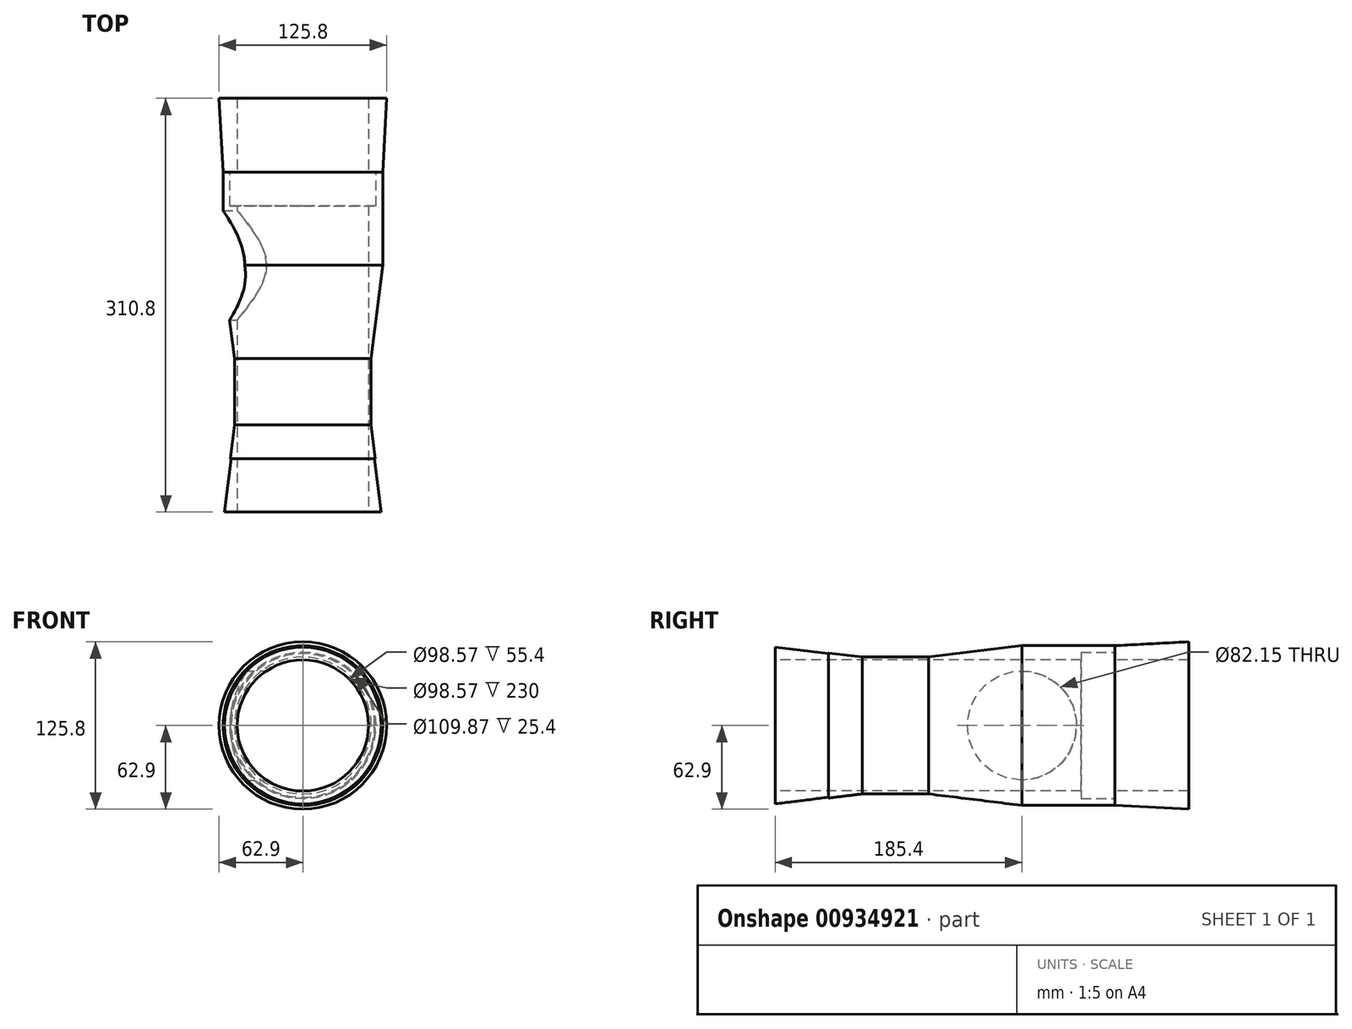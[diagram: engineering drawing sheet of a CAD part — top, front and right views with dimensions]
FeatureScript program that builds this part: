
annotation { "Feature Type Name" : "Feature", "Feature Type Description" : "" }
export const myFeature = defineFeature(function(context is Context, id is Id, definition is map)
    precondition{}
    {
        {
            var Q0;
            Q0=qCreatedBy(makeId("Front.planeOp"),FACE);
            var sketch = newSketch(context, id + "F0", { "sketchPlane" : qUnion([Q0])});
            skCircle(sketch, "E0", {"center": v(0, 0) * mm, "radius": 60 * mm});
            skSolve(sketch);
        }
        {
            var Q0;
            Q0=makeQuery(id+"F0.imprint","IMPRINT",FACE,{"disambiguationData":[TD([[makeQuery(id+"F0.imprint","IMPRINT",EDGE,{"derivedFrom":sQuery(id+"F0.wireOp",EDGE,"E0")}),1.0]])]});
            extrude(context, id + "F1", {"entities" : qUnion([Q0]), "oppositeDirection" : true, "depth" : 70 * mm, "offsetDistance" : 25.4 * mm});
        }
        {
            var Q0;
            Q0=makeQuery(id+"F1.opExtrude","CAP_FACE",FACE,{"disambiguationData":[OSD([sQuery(id+"F0.wireOp",EDGE,"E0")])],"isStart":true});
            var sketch = newSketch(context, id + "F2", { "sketchPlane" : qUnion([Q0])});
            skCircle(sketch, "E1", {"center": v(0, 0) * mm, "radius": 60 * mm});
            skSolve(sketch);
        }
        {
            var Q0;
            Q0=qSketchRegion(id+"F2",true);
            extrude(context, id + "F3", {"entities" : qUnion([Q0]), "operationType" : NewBodyOperationType.ADD, "depth" : 70 * mm, "offsetDistance" : 25.4 * mm, "hasDraft" : true, "draftAngle" : 7 * degree, "draftPullDirection" : true});
        }
        {
            var Q0;
            Q0=makeQuery(id+"F3.opExtrude","CAP_FACE",FACE,{"disambiguationData":[OSD([sQuery(id+"F2.wireOp",EDGE,"E1")])],"isStart":false});
            var sketch = newSketch(context, id + "F4", { "sketchPlane" : qUnion([Q0])});
            skCircle(sketch, "E2", {"center": v(0, 0) * mm, "radius": 53.52 * mm});
            skSolve(sketch);
        }
        {
            var Q0;
            Q0=makeQuery(id+"F1.opExtrude","CAP_FACE",FACE,{"disambiguationData":[OSD([sQuery(id+"F0.wireOp",EDGE,"E0")])],"isStart":false});
            var sketch = newSketch(context, id + "F5", { "sketchPlane" : qUnion([Q0])});
            skCircle(sketch, "E3", {"center": v(0, 0) * mm, "radius": 54.93 * mm});
            skSolve(sketch);
        }
        {
            var Q0;
            Q0=makeQuery(id+"F5.imprint","IMPRINT",FACE,{"disambiguationData":[TD([[makeQuery(id+"F5.imprint","IMPRINT",EDGE,{"derivedFrom":sQuery(id+"F5.wireOp",EDGE,"E3")}),1.0]])]});
            extrude(context, id + "F6", {"entities" : qUnion([Q0]), "operationType" : NewBodyOperationType.REMOVE, "oppositeDirection" : true, "depth" : 25.4 * mm, "offsetDistance" : 25.4 * mm});
        }
        {
            var Q0;
            Q0=makeQuery(id+"F4.imprint","IMPRINT",FACE,{"disambiguationData":[TD([[makeQuery(id+"F4.imprint","IMPRINT",EDGE,{"derivedFrom":sQuery(id+"F4.wireOp",EDGE,"E2")}),1.0]])]});
            var sketch = newSketch(context, id + "F7", { "sketchPlane" : qUnion([Q0])});
            skCircle(sketch, "E4", {"center": v(0, 0) * mm, "radius": 47.96 * mm});
            skSolve(sketch);
        }
        {
            var Q0;
            Q0=qSketchRegion(id+"F7",true);
            extrude(context, id + "F8", {"entities" : qUnion([Q0]), "operationType" : NewBodyOperationType.REMOVE, "oppositeDirection" : true, "depth" : 206 * mm, "offsetDistance" : 25.4 * mm});
        }
        {
            var Q0;
            Q0=makeQuery(id+"F1.opExtrude","CAP_FACE",FACE,{"disambiguationData":[OSD([sQuery(id+"F0.wireOp",EDGE,"E0")])],"isStart":false});
            var sketch = newSketch(context, id + "F9", { "sketchPlane" : qUnion([Q0])});
            skSolve(sketch);
        }
        {
            var Q0;
            Q0=makeQuery(id+"F9.imprint","IMPRINT",FACE,{"disambiguationData":[TD([[makeQuery(id+"F9.imprint","IMPRINT",EDGE,{"derivedFrom":makeQuery(id+"F1.opExtrude","CAP_EDGE",EDGE,{"disambiguationData":[OSD([sQuery(id+"F0.wireOp",EDGE,"E0")])],"isStart":false})}),-1.0]])]});
            var sketch = newSketch(context, id + "F10", { "sketchPlane" : qUnion([Q0])});
            skCircle(sketch, "E5", {"center": v(0, 0) * mm, "radius": 60.8 * mm});
            skSolve(sketch);
        }
        {
            var Q0;
            Q0=makeQuery(id+"F10.imprint","IMPRINT",FACE,{"disambiguationData":[TD([[makeQuery(id+"F10.imprint","IMPRINT",EDGE,{"derivedFrom":sQuery(id+"F10.wireOp",EDGE,"E5")}),1.0]])]});
            var sketch = newSketch(context, id + "F11", { "sketchPlane" : qUnion([Q0])});
            skCircle(sketch, "E6", {"center": v(0, 0) * mm, "radius": 61.4 * mm});
            skSolve(sketch);
        }
        {
            var Q0;
            Q0=makeQuery(id+"F4.imprint","IMPRINT",FACE,{"disambiguationData":[TD([[makeQuery(id+"F4.imprint","IMPRINT",EDGE,{"derivedFrom":makeQuery(id+"F3.opExtrude","CAP_EDGE",EDGE,{"disambiguationData":[OSD([sQuery(id+"F2.wireOp",EDGE,"E1")])],"isStart":false})}),1.0]])]});
            extrude(context, id + "F12", {"entities" : qUnion([Q0]), "operationType" : NewBodyOperationType.ADD, "depth" : 50 * mm, "offsetDistance" : 25.4 * mm});
        }
        {
            var Q0;
            Q0=makeQuery(id+"F12.opExtrude","CAP_FACE",FACE,{"disambiguationData":[OSD([sQuery(id+"F2.wireOp",EDGE,"E1")])],"isStart":false});
            var sketch = newSketch(context, id + "F13", { "sketchPlane" : qUnion([Q0])});
            skSolve(sketch);
        }
        {
            var Q0;
            Q0=makeQuery(id+"F13.imprint","IMPRINT",FACE,{"disambiguationData":[TD([[makeQuery(id+"F13.imprint","IMPRINT",EDGE,{"derivedFrom":makeQuery(id+"F12.opExtrude","CAP_EDGE",EDGE,{"disambiguationData":[OSD([sQuery(id+"F2.wireOp",EDGE,"E1")])],"isStart":false})}),1.0]])]});
            extrude(context, id + "F14", {"entities" : qUnion([Q0]), "operationType" : NewBodyOperationType.ADD, "depth" : 25.4 * mm, "offsetDistance" : 25.4 * mm, "hasDraft" : true, "draftAngle" : 7 * degree});
        }
        {
            var Q0;
            Q0=makeQuery(id+"F14.opExtrude","CAP_FACE",FACE,{"disambiguationData":[OSD([sQuery(id+"F2.wireOp",EDGE,"E1")])],"isStart":false});
            var sketch = newSketch(context, id + "F15", { "sketchPlane" : qUnion([Q0])});
            skCircle(sketch, "E7", {"center": v(0, 0) * mm, "radius": 53.93 * mm});
            skSolve(sketch);
        }
        {
            var Q0;
            Q0=makeQuery(id+"F15.imprint","IMPRINT",FACE,{"disambiguationData":[TD([[makeQuery(id+"F15.imprint","IMPRINT",EDGE,{"derivedFrom":sQuery(id+"F15.wireOp",EDGE,"E7")}),1.0]])]});
            extrude(context, id + "F16", {"entities" : qUnion([Q0]), "operationType" : NewBodyOperationType.ADD, "depth" : 40 * mm, "offsetDistance" : 25.4 * mm, "hasDraft" : true, "draftAngle" : 7 * degree});
        }
        {
            var Q0;
            Q0=makeQuery(id+"F11.imprint","IMPRINT",FACE,{"disambiguationData":[TD([[makeQuery(id+"F11.imprint","IMPRINT",EDGE,{"derivedFrom":makeQuery(id+"F10.imprint","IMPRINT",EDGE,{"derivedFrom":makeQuery(id+"F9.imprint","IMPRINT",EDGE,{"derivedFrom":makeQuery(id+"F1.opExtrude","CAP_EDGE",EDGE,{"disambiguationData":[OSD([sQuery(id+"F0.wireOp",EDGE,"E0")])],"isStart":false})})})}),-1.0]])]});
            extrude(context, id + "F17", {"entities" : qUnion([Q0]), "operationType" : NewBodyOperationType.ADD, "depth" : 25.4 * mm, "offsetDistance" : 25.4 * mm, "hasDraft" : true, "draftAngle" : 3 * degree});
        }
        {
            var Q0;
            Q0=makeQuery(id+"F17.opExtrude","CAP_FACE",FACE,{"disambiguationData":[OSD([sQuery(id+"F0.wireOp",EDGE,"E0")])],"isStart":false});
            var sketch = newSketch(context, id + "F18", { "sketchPlane" : qUnion([Q0])});
            skCircle(sketch, "E8", {"center": v(0, 0) * mm, "radius": 61.43 * mm});
            skSolve(sketch);
        }
        {
            var Q0;
            Q0=makeQuery(id+"F18.imprint","IMPRINT",FACE,{"disambiguationData":[TD([[makeQuery(id+"F18.imprint","IMPRINT",EDGE,{"derivedFrom":makeQuery(id+"F17.opExtrude","CAP_EDGE",EDGE,{"disambiguationData":[OSD([sQuery(id+"F0.wireOp",EDGE,"E0")])],"isStart":false})}),-1.0]])]});
            extrude(context, id + "F19", {"entities" : qUnion([Q0]), "operationType" : NewBodyOperationType.ADD, "depth" : 30 * mm, "offsetDistance" : 25.4 * mm, "hasDraft" : true, "draftAngle" : 3 * degree});
        }
        {
            var Q0;
            Q0=makeQuery(id+"F16.opExtrude","CAP_FACE",FACE,{"disambiguationData":[OSD([sQuery(id+"F15.wireOp",EDGE,"E7")])],"isStart":false});
            var sketch = newSketch(context, id + "F20", { "sketchPlane" : qUnion([Q0])});
            skCircle(sketch, "E9", {"center": v(0, 0) * mm, "radius": 46.55 * mm});
            skSolve(sketch);
        }
        {
            var Q0;
            Q0 = qSketchRegion(id + "F20", true);
            extrude(context, id + "F21", {"entities" : qUnion([Q0]), "operationType" : NewBodyOperationType.REMOVE, "oppositeDirection" : true, "depth" : 374.4 * mm, "offsetDistance" : 25.4 * mm});
        }
        {
            var Q0;
            Q0=makeQuery(id+"F16.opExtrude","CAP_FACE",FACE,{"disambiguationData":[OSD([sQuery(id+"F15.wireOp",EDGE,"E7")])],"isStart":false});
            var sketch = newSketch(context, id + "F22", { "sketchPlane" : qUnion([Q0])});
            skCircle(sketch, "E10", {"center": v(0, 0) * mm, "radius": 49.28 * mm});
            skSolve(sketch);
        }
        {
            var Q0;
            Q0 = qSketchRegion(id + "F22", true);
            extrude(context, id + "F23", {"entities" : qUnion([Q0]), "operationType" : NewBodyOperationType.REMOVE, "oppositeDirection" : true, "depth" : 359.92 * mm, "offsetDistance" : 25.4 * mm});
        }
        {
            var Q0;
            Q0=qCreatedBy(makeId("Right.planeOp"),FACE);
            var sketch = newSketch(context, id + "F24", { "sketchPlane" : qUnion([Q0])});
            skCircle(sketch, "E11", {"center": v(0, 0) * mm, "radius": 41.07 * mm});
            skSolve(sketch);
        }
        {
            var Q0;
            Q0 = qSketchRegion(id + "F24", true);
            extrude(context, id + "F25", {"entities" : qUnion([Q0]), "operationType" : NewBodyOperationType.REMOVE, "oppositeDirection" : true, "depth" : 101.85 * mm, "offsetDistance" : 25.4 * mm});
        }
    });
